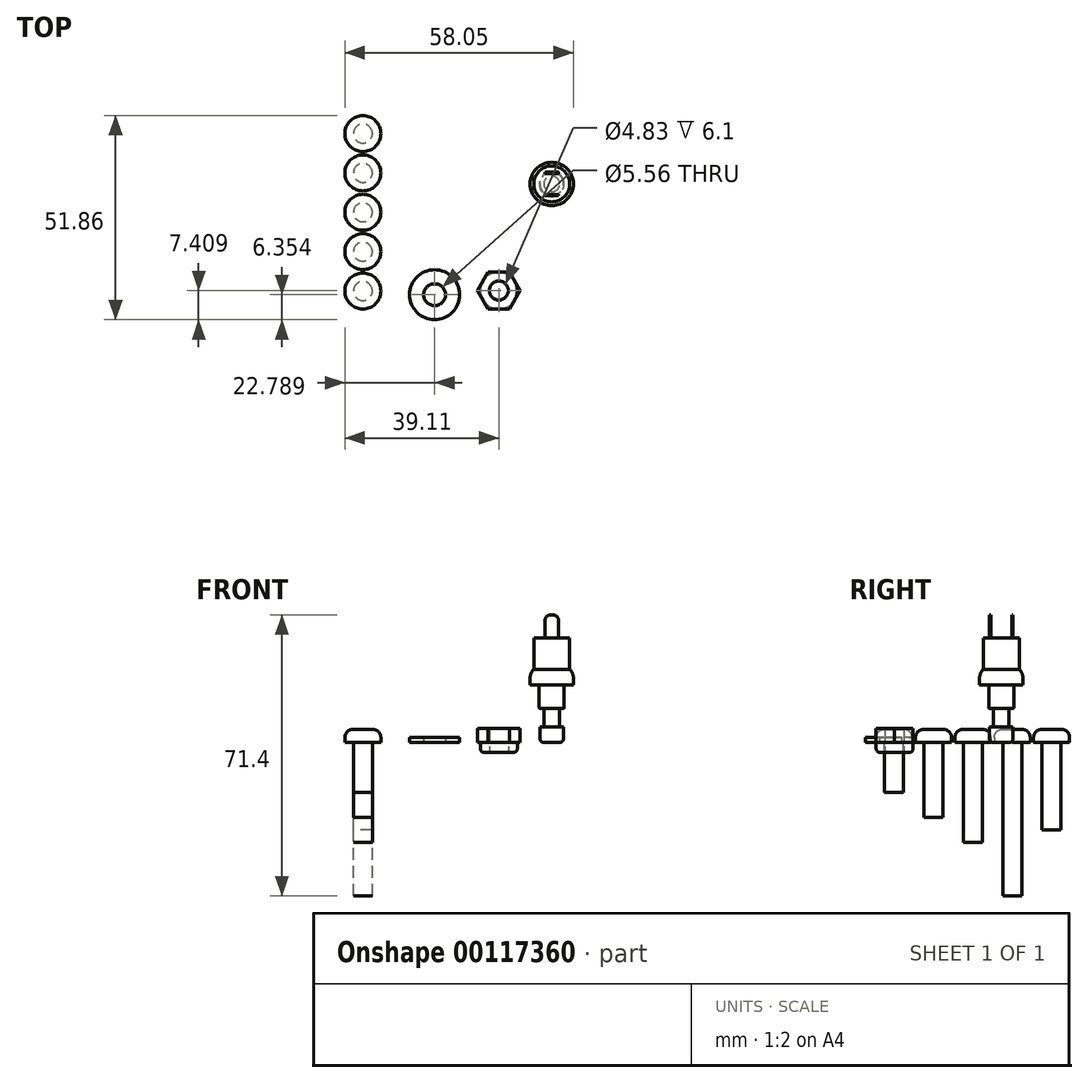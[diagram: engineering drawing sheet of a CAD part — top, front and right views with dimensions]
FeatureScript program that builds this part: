
annotation { "Feature Type Name" : "Feature", "Feature Type Description" : "" }
export const myFeature = defineFeature(function(context is Context, id is Id, definition is map)
    precondition{}
    {
        {
            var Q0;
            Q0=qCreatedBy(makeId("Top.planeOp"),FACE);
            var sketch = newSketch(context, id + "F0", { "sketchPlane" : qUnion([Q0])});
            skCircle(sketch, "E0", {"center": v(0, 0) * mm, "radius": 3 * mm});
            skSolve(sketch);
        }
        {
            var Q0;
            Q0=qSketchRegion(id+"F0",true);
            extrude(context, id + "F1", {"entities" : qUnion([Q0]), "depth" : 4 * mm});
        }
        {
            var Q0;
            Q0=makeQuery(id+"F1.opExtrude","CAP_FACE",FACE,{"disambiguationData":[OSD([sQuery(id+"F0.wireOp",EDGE,"E0")])],"isStart":false});
            var sketch = newSketch(context, id + "F2", { "sketchPlane" : qUnion([Q0])});
            skCircle(sketch, "E1", {"center": v(0, 0) * mm, "radius": 2 * mm});
            skSolve(sketch);
        }
        {
            var Q0;
            Q0=qSketchRegion(id+"F2",true);
            extrude(context, id + "F3", {"entities" : qUnion([Q0]), "operationType" : NewBodyOperationType.ADD, "depth" : 4.6 * mm});
        }
        {
            var Q0;
            Q0=makeQuery(id+"F3.opExtrude","CAP_FACE",FACE,{"disambiguationData":[OSD([sQuery(id+"F2.wireOp",EDGE,"E1")])],"isStart":false});
            var sketch = newSketch(context, id + "F4", { "sketchPlane" : qUnion([Q0])});
            skCircle(sketch, "E2", {"center": v(0, 0) * mm, "radius": 3.17 * mm});
            skSolve(sketch);
        }
        {
            var Q0;
            Q0=qSketchRegion(id+"F4",true);
            extrude(context, id + "F5", {"entities" : qUnion([Q0]), "operationType" : NewBodyOperationType.ADD, "depth" : 6 * mm});
        }
        {
            var Q0;
            Q0=makeQuery(id+"F5.opExtrude","CAP_FACE",FACE,{"disambiguationData":[OSD([sQuery(id+"F4.wireOp",EDGE,"E2")])],"isStart":false});
            var sketch = newSketch(context, id + "F6", { "sketchPlane" : qUnion([Q0])});
            skCircle(sketch, "E3", {"center": v(0, 0) * mm, "radius": 5.5 * mm});
            skSolve(sketch);
        }
        {
            var Q0;
            Q0=qSketchRegion(id+"F6",true);
            extrude(context, id + "F7", {"entities" : qUnion([Q0]), "operationType" : NewBodyOperationType.ADD, "depth" : 4 * mm});
        }
        {
            var Q0;
            Q0=makeQuery(id+"F7.opExtrude","CAP_FACE",FACE,{"disambiguationData":[OSD([sQuery(id+"F6.wireOp",EDGE,"E3")])],"isStart":false});
            var sketch = newSketch(context, id + "F8", { "sketchPlane" : qUnion([Q0])});
            skCircle(sketch, "E4", {"center": v(0, 0) * mm, "radius": 4.56 * mm});
            skSolve(sketch);
        }
        {
            var Q0;
            Q0=makeQuery(id+"F8.imprint","IMPRINT",FACE,{"disambiguationData":[TD([[makeQuery(id+"F8.imprint","IMPRINT",EDGE,{"derivedFrom":sQuery(id+"F8.wireOp",EDGE,"E4")}),1.0]])]});
            extrude(context, id + "F9", {"entities" : qUnion([Q0]), "operationType" : NewBodyOperationType.ADD, "depth" : 8 * mm});
        }
        {
            var Q0;
            Q0=makeQuery(id+"F7.opExtrude","CAP_EDGE",EDGE,{"disambiguationData":[OSD([sQuery(id+"F6.wireOp",EDGE,"E3")])],"isStart":false});
            fillet(context, id + "F10", {"entities" : qUnion([Q0]), "radius" : 3.2 * mm, "tangentPropagation" : true, "allowEdgeOverflow" : false});
        }
        {
            var Q0;
            Q0=makeQuery(id+"F1.opExtrude","CAP_EDGE",EDGE,{"disambiguationData":[OSD([sQuery(id+"F0.wireOp",EDGE,"E0")])],"isStart":true});
            fillet(context, id + "F11", {"entities" : qUnion([Q0]), "radius" : 1 * mm, "tangentPropagation" : true, "allowEdgeOverflow" : false});
        }
        {
            var Q0;
            Q0=makeQuery(id+"F5.opExtrude","CAP_EDGE",EDGE,{"disambiguationData":[OSD([sQuery(id+"F4.wireOp",EDGE,"E2")])],"isStart":true});
            fillet(context, id + "F12", {"entities" : qUnion([Q0]), "radius" : .3 * mm, "tangentPropagation" : true, "allowEdgeOverflow" : false});
        }
        {
            var Q0;
            Q0=makeQuery(id+"F9.opExtrude","CAP_FACE",FACE,{"disambiguationData":[OSD([sQuery(id+"F8.wireOp",EDGE,"E4")])],"isStart":false});
            var sketch = newSketch(context, id + "F13", { "sketchPlane" : qUnion([Q0])});
            skLineSegment(sketch, "E5.rect.bottom", {"start": v(1.75, 2.96) * mm, "end": v(-1.75, 2.96) * mm});
            skLineSegment(sketch, "E5.rect.top", {"start": v(1.75, -2.96) * mm, "end": v(-1.75, -2.96) * mm});
            skLineSegment(sketch, "E5.rect.left", {"start": v(1.75, 2.96) * mm, "end": v(1.75, 2.66) * mm});
            skLineSegment(sketch, "E5.rect.right", {"start": v(-1.75, 2.96) * mm, "end": v(-1.75, 2.66) * mm});
            skPoint(sketch, "E5.rect.middle", {"position": v(0, 0) * mm});
            skLineSegment(sketch, "E6", {"start": v(-1.75, -2.66) * mm, "end": v(1.75, -2.66) * mm});
            skLineSegment(sketch, "E7", {"start": v(-1.75, 2.66) * mm, "end": v(1.75, 2.66) * mm});
            skLineSegment(sketch, "E8.trimOffspring", {"start": v(-1.75, -2.66) * mm, "end": v(-1.75, -2.96) * mm});
            skLineSegment(sketch, "E9.trimOffspring", {"start": v(1.75, -2.66) * mm, "end": v(1.75, -2.96) * mm});
            skSolve(sketch);
        }
        {
            var Q0;
            Q0=qSketchRegion(id+"F13",true);
            extrude(context, id + "F14", {"entities" : qUnion([Q0]), "operationType" : NewBodyOperationType.ADD, "depth" : 5.8 * mm});
        }
        {
            var Q0;
            Q0=makeQuery(id+"F14.opExtrude","CAP_EDGE",EDGE,{"disambiguationData":[OSD([sQuery(id+"F13.wireOp",EDGE,"E5.rect.left")])],"isStart":false});
            var Q1;
            Q1=makeQuery(id+"F14.opExtrude","CAP_EDGE",EDGE,{"disambiguationData":[OSD([sQuery(id+"F13.wireOp",EDGE,"E9.trimOffspring")])],"isStart":false});
            var Q2;
            Q2=makeQuery(id+"F14.opExtrude","CAP_EDGE",EDGE,{"disambiguationData":[OSD([sQuery(id+"F13.wireOp",EDGE,"E8.trimOffspring")])],"isStart":false});
            var Q3;
            Q3=makeQuery(id+"F14.opExtrude","CAP_EDGE",EDGE,{"disambiguationData":[OSD([sQuery(id+"F13.wireOp",EDGE,"E5.rect.right")])],"isStart":false});
            fillet(context, id + "F15", {"entities" : qUnion([Q0, Q1, Q2, Q3]), "radius" : 1.5 * mm, "tangentPropagation" : true, "allowEdgeOverflow" : false});
        }
        {
            var Q0;
            Q0=qCreatedBy(makeId("Top.planeOp"),FACE);
            var sketch = newSketch(context, id + "F16", { "sketchPlane" : qUnion([Q0])});
            skCircle(sketch, "E10", {"center": v(-47.98, -27.21) * mm, "radius": 2.41 * mm});
            skCircle(sketch, "E11", {"center": v(-47.98, -27.21) * mm, "radius": 4.57 * mm});
            skSolve(sketch);
        }
        {
            var Q0;
            Q0=makeQuery(id+"F16.imprint","IMPRINT",FACE,{"disambiguationData":[TD([[makeQuery(id+"F16.imprint","IMPRINT",EDGE,{"derivedFrom":sQuery(id+"F16.wireOp",EDGE,"E10")}),1.0]])]});
            var Q1;
            Q1=makeQuery(id+"F16.imprint","IMPRINT",FACE,{"disambiguationData":[TD([[makeQuery(id+"F16.imprint","IMPRINT",EDGE,{"derivedFrom":sQuery(id+"F16.wireOp",EDGE,"E10")}),-1.0]])]});
            extrude(context, id + "F17", {"entities" : qUnion([Q0, Q1]), "depth" : 3.3 * mm});
        }
        {
            var Q0;
            Q0=makeQuery(id+"F17.opExtrude","CAP_EDGE",EDGE,{"disambiguationData":[OSD([sQuery(id+"F16.wireOp",EDGE,"E11")])],"isStart":false});
            fillet(context, id + "F18", {"entities" : qUnion([Q0]), "radius" : 2 * mm, "tangentPropagation" : true, "allowEdgeOverflow" : false});
        }
        {
            var Q0;
            Q0=makeQuery(id+"F16.imprint","IMPRINT",FACE,{"disambiguationData":[TD([[makeQuery(id+"F16.imprint","IMPRINT",EDGE,{"derivedFrom":sQuery(id+"F16.wireOp",EDGE,"E10")}),1.0]])]});
            extrude(context, id + "F19", {"entities" : qUnion([Q0]), "operationType" : NewBodyOperationType.ADD, "oppositeDirection" : true, "depth" : 1 * mm});
        }
        {
            var Q0;
            Q0=makeQuery(id+"F17.opExtrude","SWEPT_BODY",BODY,{"disambiguationData":[OSD([sQuery(id+"F16.wireOp",EDGE,"E11")])]});
            transform(context, id + "F20", {"entities" : qUnion([Q0]), "transformType" : TransformType.TRANSLATION_3D, "dx" : 0 * mm, "dy" : 10 * mm, "dz" : 0 * mm, "makeCopy" : true});
        }
        {
            var Q0;
            Q0=makeQuery(id+"F19.opExtrude","CAP_FACE",FACE,{"disambiguationData":[OSD([sQuery(id+"F16.wireOp",EDGE,"E10")])],"isStart":false});
            extrude(context, id + "F21", {"entities" : qUnion([Q0]), "operationType" : NewBodyOperationType.ADD, "depth" : 11.7 * mm});
        }
        {
            var Q0;
            Q0=makeQuery(id+"F20.opPattern","COPY",BODY,{"derivedFrom":makeQuery(id+"F17.opExtrude","SWEPT_BODY",BODY,{"disambiguationData":[OSD([sQuery(id+"F16.wireOp",EDGE,"E11")])]}),"instanceName":"1"});
            transform(context, id + "F22", {"entities" : qUnion([Q0]), "transformType" : TransformType.TRANSLATION_3D, "dx" : 0 * mm, "dy" : 10 * mm, "dz" : 0 * mm, "makeCopy" : true});
        }
        {
            var Q0;
            Q0=makeQuery(id+"F20.opPattern","COPY",FACE,{"derivedFrom":makeQuery(id+"F19.opExtrude","CAP_FACE",FACE,{"disambiguationData":[OSD([sQuery(id+"F16.wireOp",EDGE,"E10")])],"isStart":false}),"instanceName":"1"});
            extrude(context, id + "F23", {"entities" : qUnion([Q0]), "operationType" : NewBodyOperationType.ADD, "depth" : 18.05 * mm});
        }
        {
            var Q0;
            Q0=makeQuery(id+"F22.opPattern","COPY",BODY,{"derivedFrom":makeQuery(id+"F20.opPattern","COPY",BODY,{"derivedFrom":makeQuery(id+"F17.opExtrude","SWEPT_BODY",BODY,{"disambiguationData":[OSD([sQuery(id+"F16.wireOp",EDGE,"E11")])]}),"instanceName":"1"}),"instanceName":"1"});
            transform(context, id + "F24", {"entities" : qUnion([Q0]), "transformType" : TransformType.TRANSLATION_3D, "dx" : 0 * mm, "dy" : 10 * mm, "dz" : 0 * mm, "makeCopy" : true});
        }
        {
            var Q0;
            Q0=makeQuery(id+"F22.opPattern","COPY",FACE,{"derivedFrom":makeQuery(id+"F20.opPattern","COPY",FACE,{"derivedFrom":makeQuery(id+"F19.opExtrude","CAP_FACE",FACE,{"disambiguationData":[OSD([sQuery(id+"F16.wireOp",EDGE,"E10")])],"isStart":false}),"instanceName":"1"}),"instanceName":"1"});
            extrude(context, id + "F25", {"entities" : qUnion([Q0]), "operationType" : NewBodyOperationType.ADD, "depth" : 24.4 * mm});
        }
        {
            var Q0;
            Q0=makeQuery(id+"F24.opPattern","COPY",BODY,{"derivedFrom":makeQuery(id+"F22.opPattern","COPY",BODY,{"derivedFrom":makeQuery(id+"F20.opPattern","COPY",BODY,{"derivedFrom":makeQuery(id+"F17.opExtrude","SWEPT_BODY",BODY,{"disambiguationData":[OSD([sQuery(id+"F16.wireOp",EDGE,"E11")])]}),"instanceName":"1"}),"instanceName":"1"}),"instanceName":"1"});
            transform(context, id + "F26", {"entities" : qUnion([Q0]), "transformType" : TransformType.TRANSLATION_3D, "dx" : 0 * mm, "dy" : 10 * mm, "dz" : 0 * mm, "makeCopy" : true});
        }
        {
            var Q0;
            Q0=makeQuery(id+"F24.opPattern","COPY",FACE,{"derivedFrom":makeQuery(id+"F22.opPattern","COPY",FACE,{"derivedFrom":makeQuery(id+"F20.opPattern","COPY",FACE,{"derivedFrom":makeQuery(id+"F19.opExtrude","CAP_FACE",FACE,{"disambiguationData":[OSD([sQuery(id+"F16.wireOp",EDGE,"E10")])],"isStart":false}),"instanceName":"1"}),"instanceName":"1"}),"instanceName":"1"});
            extrude(context, id + "F27", {"entities" : qUnion([Q0]), "operationType" : NewBodyOperationType.ADD, "depth" : 38 * mm});
        }
        {
            var Q0;
            Q0=qCreatedBy(makeId("Top.planeOp"),FACE);
            var sketch = newSketch(context, id + "F28", { "sketchPlane" : qUnion([Q0])});
            skCircle(sketch, "E12", {"center": v(-29.76, -28.15) * mm, "radius": 2.78 * mm});
            skCircle(sketch, "E13", {"center": v(-29.76, -28.15) * mm, "radius": 6.35 * mm});
            skSolve(sketch);
        }
        {
            var Q0;
            Q0=qSketchRegion(id+"F28",true);
            extrude(context, id + "F29", {"entities" : qUnion([Q0]), "depth" : 1.23 * mm});
        }
        {
            var Q0;
            Q0=qCreatedBy(makeId("Top.planeOp"),FACE);
            var sketch = newSketch(context, id + "F30", { "sketchPlane" : qUnion([Q0])});
            skCircle(sketch, "E14.cCircle", {"center": v(-13.44, -27.1) * mm, "radius": 4.7 * mm, "construction": true});
            skLineSegment(sketch, "E14.0", {"start": v(-16.15, -22.4) * mm, "end": v(-10.73, -22.4) * mm});
            skLineSegment(sketch, "E14.1", {"start": v(-10.73, -22.4) * mm, "end": v(-8.01, -27.1) * mm});
            skLineSegment(sketch, "E14.2", {"start": v(-8.01, -27.1) * mm, "end": v(-10.73, -31.79) * mm});
            skLineSegment(sketch, "E14.3", {"start": v(-10.73, -31.79) * mm, "end": v(-16.15, -31.79) * mm});
            skLineSegment(sketch, "E14.4", {"start": v(-16.15, -31.79) * mm, "end": v(-18.87, -27.1) * mm});
            skLineSegment(sketch, "E14.5", {"start": v(-18.87, -27.1) * mm, "end": v(-16.15, -22.4) * mm});
            skPoint(sketch, "E14.0.midPoint", {"position": v(-13.44, -22.4) * mm});
            skCircle(sketch, "E15", {"center": v(-13.44, -27.1) * mm, "radius": 2.41 * mm});
            skCircle(sketch, "E16", {"center": v(-13.44, -27.1) * mm, "radius": 4.7 * mm});
            skSolve(sketch);
        }
        {
            var Q0;
            Q0=qSketchRegion(id+"F30",true);
            extrude(context, id + "F31", {"entities" : qUnion([Q0]), "depth" : 3.56 * mm});
        }
        {
            var Q0;
            Q0=makeQuery(id+"F30.imprint","IMPRINT",FACE,{"disambiguationData":[TD([[makeQuery(id+"F30.imprint","IMPRINT",EDGE,{"derivedFrom":sQuery(id+"F30.wireOp",EDGE,"E15")}),-1.0]])]});
            extrude(context, id + "F32", {"entities" : qUnion([Q0]), "operationType" : NewBodyOperationType.ADD, "oppositeDirection" : true, "depth" : 2.54 * mm});
        }
        {
            var Q0;
            Q0=makeQuery(id+"F32.opExtrude","CAP_EDGE",EDGE,{"disambiguationData":[OSD([sQuery(id+"F30.wireOp",EDGE,"E16")])],"isStart":false});
            fillet(context, id + "F33", {"entities" : qUnion([Q0]), "radius" : 1 * mm, "tangentPropagation" : true, "allowEdgeOverflow" : false});
        }
        {
            var Q0;
            Q0=makeQuery(id+"F26.opPattern","COPY",FACE,{"derivedFrom":makeQuery(id+"F24.opPattern","COPY",FACE,{"derivedFrom":makeQuery(id+"F22.opPattern","COPY",FACE,{"derivedFrom":makeQuery(id+"F20.opPattern","COPY",FACE,{"derivedFrom":makeQuery(id+"F19.opExtrude","CAP_FACE",FACE,{"disambiguationData":[OSD([sQuery(id+"F16.wireOp",EDGE,"E10")])],"isStart":false}),"instanceName":"1"}),"instanceName":"1"}),"instanceName":"1"}),"instanceName":"1"});
            extrude(context, id + "F34", {"entities" : qUnion([Q0]), "operationType" : NewBodyOperationType.ADD, "depth" : 21.23 * mm});
        }
    });
